# Revit family: NBS_Senator_DmstcChrs_Circo
name_source: partatom
category: Furniture
revit_build: Autodesk Revit 2018 (Build: 20190510_1515(x64)
units: mm (PartAtom-declared; Revit-internal decimal feet)

## family parameters
Always vertical = Yes
Cut with Voids When Loaded = No
Room Calculation Point = No
Shared = No
Work Plane-Based = No

## types (2) — shared parameters
AssetType = Movable
Category = Pr_40_50_12_22:Dining chairs
CodePerformance = EN 16139:2013, LI GS certificate, ANSI/BIFMA X5 1:2001
Color = Black, light grey, polished aluminium
Description = Work chair
DurationUnit = year
ExpectedLife = 10
Features = Plastic glides, self supporting mesh back, height adjustable with free floating tilt, injection mounded 5 star plastic base
Finish = Black plastic, light grey plastic or polished aluminium
FramesColour = Black, light grey
HighestSeatingHeight = 540 mm  [stored 1.77165 ft]
IfcExportAs = IfcFurnitureType
IfcExportType = CHAIR
IsBuiltIn = No
LowestSeatingHeight = 420 mm
ManufacturerName = The Senator Group
ManufacturerURL = www.senator.co.uk
Material = Steel, fabric, aluminium casting
MeshColours = Black, grey, snow, burnt orange, fresh apple, soft cyan
NBSCertification = www.nationalbimlibrary.com/cert/fvir5kq3
NBSDescription = Domestic chairs
NBSReference = 45-35-20/365
NominalDepth = 750 mm
NominalHeight = 1010 mm
NominalLength = 700 mm
NominalWidth = 700 mm
ProductInformation = http://www.thesenatorgroup.com
SeatBackMaterial = NBS_Senator_FabricMesh _Black
SeatCushionMaterial = NBS_Senator_Fabric_Black
SeatDepth = 460 mm
SeatFrameMaterial = NBS_Senator_Plastic_Black
SeatWidth = 490 mm
SeatingHeight = 540 mm  [stored 1.77165 ft]
Size = 750 x 1010 x 700 mm
Status = UNSET
Style = Chair
SustainabilityPerformance = 100% recyclable
Uniclass2015Code = Pr_40_50_12_22
Uniclass2015Title = Dining chairs
Uniclass2015Version = Products v1.16
Version = 1
WarrantyDescription = Senator warrants that its manufactured products are free from manufacturing defects - in materials or workmanship - for a period of ten (10) years on Senator Seating ranges; and fifteen (15) years on Senator Desking ranges - exceptions are listed below. Senator will repair or replace (at Senator’s sole discretion) with comparable free of charge materials / components, any product / component, which fails under normal use in a single shift environment, as a result of a defect in the materials and / or workmanship
WarrantyDurationParts = 10
WarrantyDurationUnit = year

## per-type parameters (varying)
| type | BIMObjectName | FrameMaterial | InternalWheelMaterial | ModelNumber | Name | ShowFrameCR7 | ShowFrameCR8 | WheelMaterial |
| Circo_CR7 | NBS_TheSenatorGroup_DomesticChairs_Circo_CR7 | NBS_SenatorGroup_Aluminium_Flat_Silver | NBS_SenatorGroup_Aluminium_Flat_Silver | CR7 | DomesticChairs_Circo_CR7_TheSenatorGroup | Yes | No | NBS_SenatorGroup_Rubber_Black |
| Circo_CR8 | NBS_TheSenatorGroup_DomesticChairs_Circo_CR8 | NBS_Senator_Polished_Aluminium | NBS_Senator_Aluminium_Flat_Silver | CR8 | DomesticChairs_Circo_CR8_TheSenatorGroup | No | Yes | NBS_Senator_Rubber_Black |

note: column(s) folded — value = type name in every type: ModelReference

note: [stored X ft] marks values corroborated as IEEE doubles in the binary element streams (Revit-internal decimal feet)

## geometry (parser evidence)
native form markers: Sweep x7
no freeform markers — native parametric forms only
